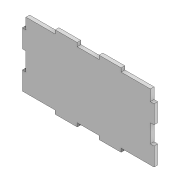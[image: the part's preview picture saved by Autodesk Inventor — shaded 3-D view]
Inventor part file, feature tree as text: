
AUTODESK INVENTOR PART (.ipt)
format: ipt  version: 2022 (Build 260153000, 153)  size: 119,808 bytes
history: native  units: mm
features: extrude x1, sketch x1
ambient origin geometry x8: Origin, YZ Plane, XZ Plane, XY Plane, X Axis, Y Axis, Z Axis, Center Point
bodies: Solid1 (feature_tree)
feature tree (2):
  extrude  "Extrusion1"  Depth=90.0mm
  sketch  "Sketch1"  dims[d0=170.0mm d1=90.0mm d2=30.0mm d3=5.0mm d4=30.0mm d5=5.0mm d6=30.0mm d7=40.0mm d8=5.0mm d9=25.0mm d10=5.0mm d11=25.0mm d12=25.0mm d13=15.0mm d14=5.0mm d15=0.0mm]
